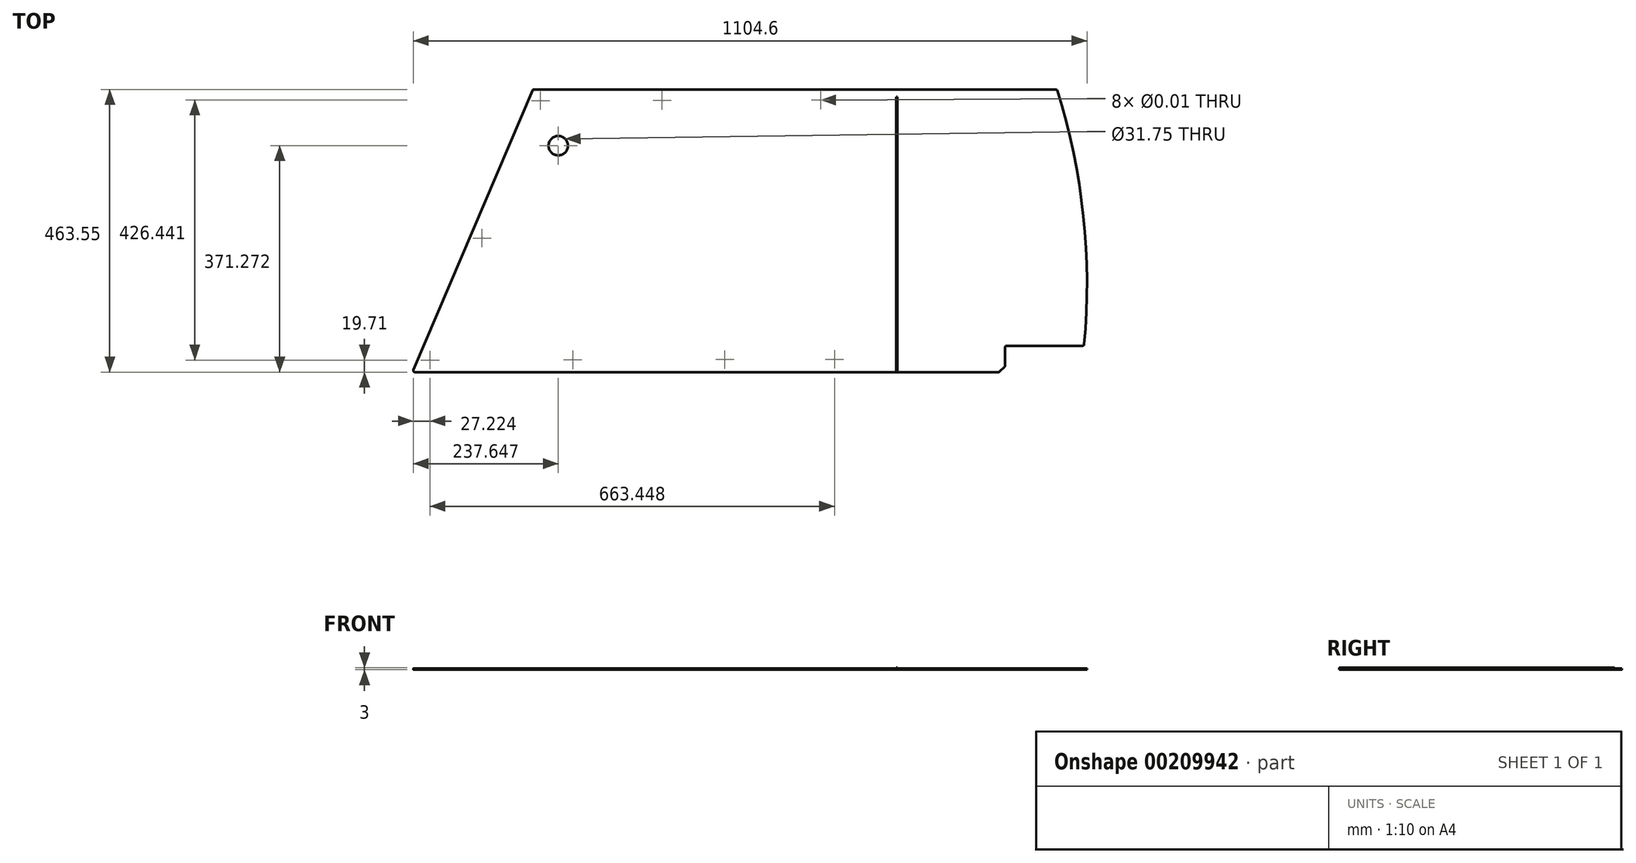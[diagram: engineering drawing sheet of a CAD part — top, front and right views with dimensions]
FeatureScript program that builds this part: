
annotation { "Feature Type Name" : "Feature", "Feature Type Description" : "" }
export const myFeature = defineFeature(function(context is Context, id is Id, definition is map)
    precondition{}
    {
        {
            var Q0;
            Q0=qCreatedBy(makeId("Top.planeOp"),FACE);
            var sketch = newSketch(context, id + "F0", { "sketchPlane" : qUnion([Q0])});
            skLineSegment(sketch, "E0", {"start": v(0, 0) * mm, "end": v(197.5, 463.55) * mm});
            skLineSegment(sketch, "E1", {"start": v(1056.54, 463.55) * mm, "end": v(197.5, 463.55) * mm});
            skArc(sketch, "E2", {"start": v(1101, 43.18) * mm, "mid": v(1100.05, 255.62) * mm, "end": v(1056.54, 463.55) * mm});
            skLineSegment(sketch, "E3", {"start": v(1101, 43.18) * mm, "end": v(971.55, 43.18) * mm});
            skLineSegment(sketch, "E4", {"start": v(971.55, 43.18) * mm, "end": v(971.55, 0) * mm});
            skLineSegment(sketch, "E5", {"start": v(971.55, 0) * mm, "end": v(0, 0) * mm});
            skSolve(sketch);
        }
        {
            var Q0;
            Q0 = qSketchRegion(id + "F0", true);
            extrude(context, id + "F1", {"entities" : qUnion([Q0]), "depth" : 3 * mm});
        }
        {
            var Q0;
            Q0=makeQuery(id+"F1.opExtrude","SWEPT_EDGE",EDGE,{"disambiguationData":[OSD([sQuery(id+"F0.wireOp",EDGE,"E4"),sQuery(id+"F0.wireOp",EDGE,"E5")])]});
            chamfer(context, id + "F2", {"entities" : qUnion([Q0]), "width" : 9.52 * mm, "tangentPropagation" : true});
        }
        {
            var Q0;
            Q0=makeQuery(id+"F1.opExtrude","CAP_FACE",FACE,{"disambiguationData":[OSD([sQuery(id+"F0.wireOp",EDGE,"E0"),sQuery(id+"F0.wireOp",EDGE,"E1"),sQuery(id+"F0.wireOp",EDGE,"E2"),sQuery(id+"F0.wireOp",EDGE,"E3"),sQuery(id+"F0.wireOp",EDGE,"E4"),sQuery(id+"F0.wireOp",EDGE,"E5")])],"isStart":false});
            var sketch = newSketch(context, id + "F3", { "sketchPlane" : qUnion([Q0])});
            skLineSegment(sketch, "E6.bottom", {"start": v(793.26, 0) * mm, "end": v(794.85, 0) * mm});
            skLineSegment(sketch, "E6.top", {"start": v(793.26, 451.37) * mm, "end": v(794.85, 451.37) * mm});
            skLineSegment(sketch, "E6.left", {"start": v(793.26, 0) * mm, "end": v(793.26, 451.37) * mm});
            skLineSegment(sketch, "E6.right", {"start": v(794.85, 0) * mm, "end": v(794.85, 451.37) * mm});
            skSolve(sketch);
        }
        {
            var Q0;
            Q0=makeQuery(id+"F3.imprint","IMPRINT",FACE,{"disambiguationData":[TD([[makeQuery(id+"F3.imprint","IMPRINT",EDGE,{"derivedFrom":sQuery(id+"F3.wireOp",EDGE,"E6.top")}),1.0]])]});
            extrude(context, id + "F4", {"entities" : qUnion([Q0]), "operationType" : NewBodyOperationType.REMOVE, "oppositeDirection" : true, "depth" : 0.75 * mm});
        }
        {
            var Q0;
            Q0=makeQuery(id+"F4.boolean.opBoolean","COPY",FACE,{"derivedFrom":makeQuery(id+"F4.opExtrude","CAP_FACE",FACE,{"disambiguationData":[OSD([sQuery(id+"F0.wireOp",EDGE,"E0"),sQuery(id+"F0.wireOp",EDGE,"E1"),sQuery(id+"F0.wireOp",EDGE,"E2"),sQuery(id+"F0.wireOp",EDGE,"E3"),sQuery(id+"F0.wireOp",EDGE,"E4"),sQuery(id+"F0.wireOp",EDGE,"E5"),sQuery(id+"F3.wireOp",EDGE,"E6.top"),sQuery(id+"F3.wireOp",EDGE,"E6.left"),sQuery(id+"F3.wireOp",EDGE,"E6.right")])],"isStart":false})});
            var sketch = newSketch(context, id + "F5", { "sketchPlane" : qUnion([Q0])});
            skLineSegment(sketch, "E7", {"start": v(669.15, 446.15) * mm, "end": v(209.74, 445.03) * mm, "construction": true});
            skLineSegment(sketch, "E8", {"start": v(209.74, 445.03) * mm, "end": v(28.52, 19.71) * mm, "construction": true});
            skLineSegment(sketch, "E9", {"start": v(28.52, 19.71) * mm, "end": v(691.97, 21.03) * mm, "construction": true});
            skPoint(sketch, "E10", {"position": v(113.74, 219.72) * mm});
            skPoint(sketch, "E11", {"position": v(409.23, 445.52) * mm});
            skPoint(sketch, "E12", {"position": v(262.71, 20.18) * mm});
            skPoint(sketch, "E13", {"position": v(511.89, 20.67) * mm});
            skSolve(sketch);
        }
        {
            var Q0;
            Q0=sQuery(id+"F5.wireOp",VERTEX,"E8.start");
            var Q1;
            Q1=sQuery(id+"F5.wireOp",VERTEX,"E11");
            var Q2;
            Q2=sQuery(id+"F5.wireOp",VERTEX,"E7.start");
            var Q3;
            Q3=sQuery(id+"F5.wireOp",VERTEX,"E10");
            var Q4;
            Q4=sQuery(id+"F5.wireOp",VERTEX,"E9.start");
            var Q5;
            Q5=sQuery(id+"F5.wireOp",VERTEX,"E12");
            var Q6;
            Q6=sQuery(id+"F5.wireOp",VERTEX,"E13");
            var Q7;
            Q7=sQuery(id+"F5.wireOp",VERTEX,"E9.end");
            var Q8;
            Q8=makeQuery(id+"F1.opExtrude","SWEPT_BODY",BODY,{"disambiguationData":[OSD([sQuery(id+"F0.wireOp",EDGE,"E0"),sQuery(id+"F0.wireOp",EDGE,"E1"),sQuery(id+"F0.wireOp",EDGE,"E2"),sQuery(id+"F0.wireOp",EDGE,"E3"),sQuery(id+"F0.wireOp",EDGE,"E4"),sQuery(id+"F0.wireOp",EDGE,"E5")])]});
            hole(context, id + "F6", {"style" : HoleStyle.SIMPLE, "endStyle" : HoleEndStyle.THROUGH, "standardTappedOrClearance" : lookupTablePath({ "standard" : "ANSI", "size" : "3/8 (0.38)", "type" : "Drilled" }), "standardBlindInLast" : lookupTablePath({ "standard" : "ANSI", "size" : "3/8", "type" : "Drilled" }), "holeDiameter" : 3 / 203.2 * mm, "locations" : qUnion([Q0, Q1, Q2, Q3, Q4, Q5, Q6, Q7]), "scope" : qUnion([Q8]), "isTappedThrough" : true});
        }
        {
            var Q0;
            Q0=makeQuery(id+"F4.boolean.opBoolean","COPY",FACE,{"derivedFrom":makeQuery(id+"F4.opExtrude","CAP_FACE",FACE,{"disambiguationData":[OSD([sQuery(id+"F0.wireOp",EDGE,"E0"),sQuery(id+"F0.wireOp",EDGE,"E1"),sQuery(id+"F0.wireOp",EDGE,"E2"),sQuery(id+"F0.wireOp",EDGE,"E3"),sQuery(id+"F0.wireOp",EDGE,"E4"),sQuery(id+"F0.wireOp",EDGE,"E5"),sQuery(id+"F3.wireOp",EDGE,"E6.top"),sQuery(id+"F3.wireOp",EDGE,"E6.left"),sQuery(id+"F3.wireOp",EDGE,"E6.right")])],"isStart":false})});
            var sketch = newSketch(context, id + "F7", { "sketchPlane" : qUnion([Q0])});
            skPoint(sketch, "E14", {"position": v(238.95, 371.27) * mm});
            skSolve(sketch);
        }
        {
            var Q0;
            Q0=sQuery(id+"F7.wireOp",VERTEX,"E14");
            var Q1;
            Q1=makeQuery(id+"F1.opExtrude","SWEPT_BODY",BODY,{"disambiguationData":[OSD([sQuery(id+"F0.wireOp",EDGE,"E0"),sQuery(id+"F0.wireOp",EDGE,"E1"),sQuery(id+"F0.wireOp",EDGE,"E2"),sQuery(id+"F0.wireOp",EDGE,"E3"),sQuery(id+"F0.wireOp",EDGE,"E4"),sQuery(id+"F0.wireOp",EDGE,"E5")])]});
            hole(context, id + "F8", {"style" : HoleStyle.SIMPLE, "endStyle" : HoleEndStyle.THROUGH, "holeDiameter" : 31.75 * mm, "locations" : qUnion([Q0]), "scope" : qUnion([Q1]), "isTappedThrough" : true});
        }
        {
            var Q0;
            Q0=makeQuery(id+"F1.opExtrude","SWEPT_EDGE",EDGE,{"disambiguationData":[OSD([sQuery(id+"F0.wireOp",EDGE,"E0"),sQuery(id+"F0.wireOp",EDGE,"E1")])]});
            var Q1;
            Q1=makeQuery(id+"F1.opExtrude","SWEPT_EDGE",EDGE,{"disambiguationData":[OSD([sQuery(id+"F0.wireOp",EDGE,"E1"),sQuery(id+"F0.wireOp",EDGE,"E2")])]});
            var Q2;
            Q2=makeQuery(id+"F1.opExtrude","SWEPT_EDGE",EDGE,{"disambiguationData":[OSD([sQuery(id+"F0.wireOp",EDGE,"E2"),sQuery(id+"F0.wireOp",EDGE,"E3")])]});
            var Q3;
            Q3=makeQuery(id+"F1.opExtrude","SWEPT_EDGE",EDGE,{"disambiguationData":[OSD([sQuery(id+"F0.wireOp",EDGE,"E3"),sQuery(id+"F0.wireOp",EDGE,"E4")])]});
            var Q4;
            {var subQ0=sQuery(id+"F0.wireOp",EDGE,"E4");Q4=makeQuery(id+"F2.opChamfer","BLEND_EDGE",EDGE,{"blendedFrom":[makeQuery(id+"F1.opExtrude","SWEPT_EDGE",EDGE,{"disambiguationData":[OSD([subQ0,sQuery(id+"F0.wireOp",EDGE,"E5")])]}),makeQuery(id+"F1.opExtrude","SWEPT_FACE",FACE,{"disambiguationData":[OSD([subQ0])]})],"blendedInto":[makeQuery(id+"F1.opExtrude","SWEPT_FACE",FACE,{"disambiguationData":[OSD([subQ0])]})]});}
            var Q5;
            {var subQ0=sQuery(id+"F0.wireOp",EDGE,"E5");Q5=makeQuery(id+"F2.opChamfer","BLEND_EDGE",EDGE,{"blendedFrom":[makeQuery(id+"F1.opExtrude","SWEPT_EDGE",EDGE,{"disambiguationData":[OSD([sQuery(id+"F0.wireOp",EDGE,"E4"),subQ0])]}),makeQuery(id+"F1.opExtrude","SWEPT_FACE",FACE,{"disambiguationData":[OSD([subQ0])]})],"blendedInto":[makeQuery(id+"F1.opExtrude","SWEPT_FACE",FACE,{"disambiguationData":[OSD([subQ0])]})]});}
            var Q6;
            Q6=makeQuery(id+"F1.opExtrude","SWEPT_EDGE",EDGE,{"disambiguationData":[OSD([sQuery(id+"F0.wireOp",EDGE,"E0"),sQuery(id+"F0.wireOp",EDGE,"E5")])]});
            fillet(context, id + "F9", {"entities" : qUnion([Q0, Q1, Q2, Q3, Q4, Q5, Q6]), "radius" : 2.54 * mm, "tangentPropagation" : true, "allowEdgeOverflow" : false});
        }
    });
